# Revit family: 712-4220-001-DN80-150
name_source: partatom
category: Pipe Accessories
units: mm (PartAtom-declared; Revit-internal decimal feet)

## family parameters
Always vertical = Yes
Cut with Voids When Loaded = No
Part Type = Valve - Breaks Into
Round Connector Dimension = Use Diameter
Shared = No
Work Plane-Based = No

## types (3) — shared parameters
Body_wallthickness = 10 mm  [stored 0.0328084 ft]
DN080_PN10/16 = 712-0080-42-201
DN100_PN10/16 = 712-0100-42-201
DN150_PN10/16 = 712-0150-42-201
Description_ = AVK FLANGED PIPE W/LOOSE FLANGES
L = 200 mm  [stored 0.656168 ft]
RF_Thick = 3 mm  [stored 0.00984252 ft]
Search_Table = 712-4220-001-DN80-150
URL product pages = https://www.avkvalves.com

## per-type parameters (varying)
| type | FOD | Flange_thickness | ID(Radius) | Nominal Diameter (DN) | Rf_Dia |
| DN080_PN10/16 | 100 mm  [stored 0.328084 ft] | 19 mm  [stored 0.062336 ft] | 40 mm  [stored 0.131234 ft] | 80 mm  [stored 0.262467 ft] | 66 mm  [stored 0.216535 ft] |
| DN100_PN10/16 | 110 mm  [stored 0.360892 ft] | 19 mm  [stored 0.062336 ft] | 50 mm  [stored 0.164042 ft] | 100 mm  [stored 0.328084 ft] | 78 mm  [stored 0.255906 ft] |
| DN150_PN10/16 | 143 mm | 20 mm  [stored 0.0656168 ft] | 75 mm  [stored 0.246063 ft] | 150 mm  [stored 0.492126 ft] | 106 mm |

note: [stored X ft] marks values corroborated as IEEE doubles in the binary element streams (Revit-internal decimal feet)

## geometry (parser evidence)
native form markers: Sweep x13
no freeform markers — native parametric forms only
